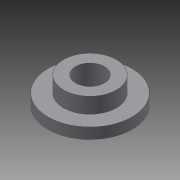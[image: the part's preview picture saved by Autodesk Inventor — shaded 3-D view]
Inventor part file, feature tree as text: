
AUTODESK INVENTOR PART (.ipt)
format: ipt  version: 2014 (Build 180170000, 170)  size: 86,528 bytes
history: native  units: mm
features: extrude x3, sketch x3
ambient origin geometry x8: Origin, YZ Plane, XZ Plane, XY Plane, X Axis, Y Axis, Z Axis, Center Point
bodies: Solid1 (feature_tree)
feature tree (6):
  extrude  "Extrusion1"  Depth=4.5mm TaperAngle=0.0deg
  extrude  "Extrusion2"  Depth=6.5mm TaperAngle=0.0deg
  extrude  "Extrusion3"  Depth=6.5mm TaperAngle=0.0deg
  sketch  "Sketch1"  dims[d0=35.0mm d1=4.5mm d2=0.0mm]
  sketch  "Sketch2"  dims[d3=22.0mm d4=6.5mm d5=0.0mm]
  sketch  "Sketch3"  dims[d6=12.0mm d7=6.5mm d8=0.0mm]
